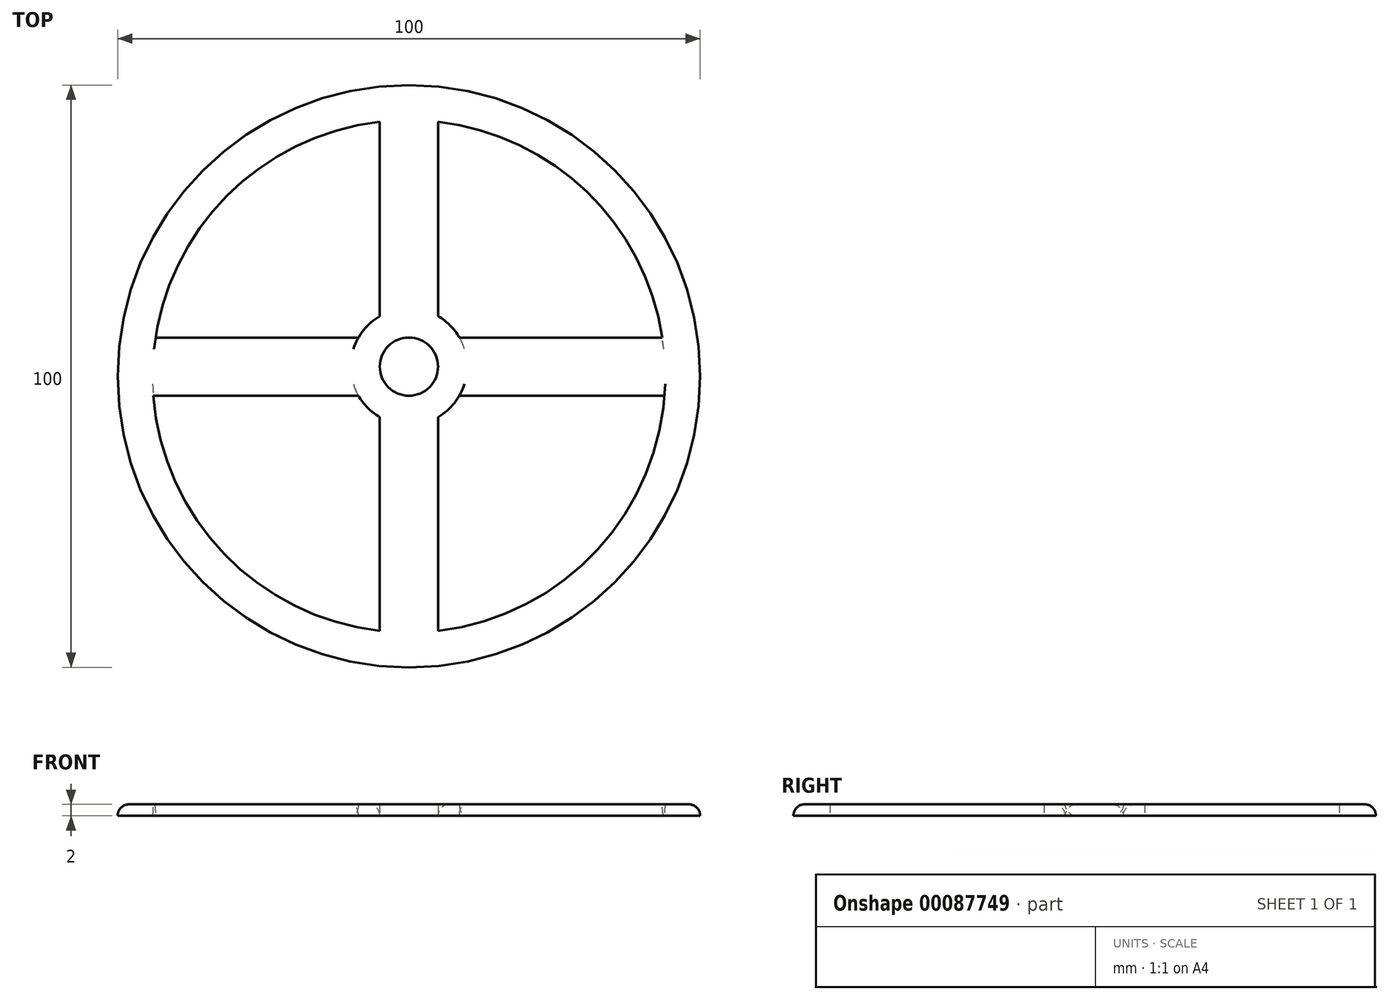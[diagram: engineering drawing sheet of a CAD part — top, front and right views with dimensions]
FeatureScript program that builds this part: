
annotation { "Feature Type Name" : "Feature", "Feature Type Description" : "" }
export const myFeature = defineFeature(function(context is Context, id is Id, definition is map)
    precondition{}
    {
        {
            var Q0;
            Q0=qCreatedBy(makeId("Top.planeOp"),FACE);
            var sketch = newSketch(context, id + "F0", { "sketchPlane" : qUnion([Q0])});
            skCircle(sketch, "E0", {"center": v(0, -1.66) * mm, "radius": 50 * mm});
            skArc(sketch, "E1.0", {"start": v(-43.87, -5) * mm, "mid": v(-31.7, -32.18) * mm, "end": v(-5, -45.38) * mm});
            skCircle(sketch, "E2", {"center": v(0, 0) * mm, "radius": 5 * mm});
            skLineSegment(sketch, "E3", {"start": v(8.66, -5) * mm, "end": v(43.87, -5) * mm});
            skLineSegment(sketch, "E4", {"start": v(5, -8.66) * mm, "end": v(5, -45.38) * mm});
            skArc(sketch, "E5.0", {"start": v(8.66, 5) * mm, "mid": v(7.07, 7.07) * mm, "end": v(5, 8.66) * mm});
            skArc(sketch, "E6.trimOffspring", {"start": v(-5, 42.05) * mm, "mid": v(-30.51, 30.04) * mm, "end": v(-43.5, 5) * mm});
            skArc(sketch, "E7.trimOffspring", {"start": v(43.5, 5) * mm, "mid": v(30.51, 30.04) * mm, "end": v(5, 42.05) * mm});
            skArc(sketch, "E8.trimOffspring", {"start": v(5, -45.38) * mm, "mid": v(31.7, -32.18) * mm, "end": v(43.87, -5) * mm});
            skLineSegment(sketch, "E9.trimOffspring", {"start": v(-8.66, -5) * mm, "end": v(-43.87, -5) * mm});
            skLineSegment(sketch, "E10.trimOffspring", {"start": v(-5, -8.66) * mm, "end": v(-5, -45.38) * mm});
            skPoint(sketch, "E11.orphan", {"position": v(0, -5) * mm});
            skArc(sketch, "E12.trimOffspring", {"start": v(5, -8.66) * mm, "mid": v(7.07, -7.07) * mm, "end": v(8.66, -5) * mm});
            skArc(sketch, "E13.trimOffspring", {"start": v(-8.66, -5) * mm, "mid": v(-7.07, -7.07) * mm, "end": v(-5, -8.66) * mm});
            skLineSegment(sketch, "E14.trimOffspring", {"start": v(-5, 8.66) * mm, "end": v(-5, 42.05) * mm});
            skLineSegment(sketch, "E15.trimOffspring", {"start": v(-8.66, 5) * mm, "end": v(-43.5, 5) * mm});
            skPoint(sketch, "E16.start.orphan", {"position": v(-5, 0) * mm});
            skLineSegment(sketch, "E17.trimOffspring", {"start": v(8.66, 5) * mm, "end": v(43.5, 5) * mm});
            skLineSegment(sketch, "E18.trimOffspring", {"start": v(5, 8.66) * mm, "end": v(5, 42.05) * mm});
            skArc(sketch, "E19.trimOffspring", {"start": v(-5, 8.66) * mm, "mid": v(-7.07, 7.07) * mm, "end": v(-8.66, 5) * mm});
            skPoint(sketch, "E20.start.orphan", {"position": v(5, 0) * mm});
            skPoint(sketch, "E21.start.orphan", {"position": v(0, 5) * mm});
            skSolve(sketch);
        }
        {
            var Q0;
            Q0=makeQuery(id+"F0.imprint","IMPRINT",FACE,{"disambiguationData":[TD([[makeQuery(id+"F0.imprint","IMPRINT",EDGE,{"derivedFrom":sQuery(id+"F0.wireOp",EDGE,"E0")}),1.0]])]});
            extrude(context, id + "F1", {"entities" : qUnion([Q0]), "depth" : 2 * mm});
        }
        {
            var Q0;
            Q0=makeQuery(id+"F1.opExtrude","CAP_EDGE",EDGE,{"disambiguationData":[OSD([sQuery(id+"F0.wireOp",EDGE,"E0")])],"isStart":false});
            var Q1;
            Q1=makeQuery(id+"F1.opExtrude","CAP_EDGE",EDGE,{"disambiguationData":[OSD([sQuery(id+"F0.wireOp",EDGE,"E17.trimOffspring")])],"isStart":true});
            var Q2;
            Q2=makeQuery(id+"F1.opExtrude","CAP_EDGE",EDGE,{"disambiguationData":[OSD([sQuery(id+"F0.wireOp",EDGE,"E9.trimOffspring")])],"isStart":true});
            var Q3;
            Q3=makeQuery(id+"F1.opExtrude","CAP_EDGE",EDGE,{"disambiguationData":[OSD([sQuery(id+"F0.wireOp",EDGE,"E15.trimOffspring")])],"isStart":false});
            var Q4;
            Q4=makeQuery(id+"F1.opExtrude","CAP_EDGE",EDGE,{"disambiguationData":[OSD([sQuery(id+"F0.wireOp",EDGE,"E3")])],"isStart":false});
            var Q5;
            Q5=makeQuery(id+"F1.opExtrude","CAP_EDGE",EDGE,{"disambiguationData":[OSD([sQuery(id+"F0.wireOp",EDGE,"E2")])],"isStart":false});
            fillet(context, id + "F2", {"entities" : qUnion([Q0, Q1, Q2, Q3, Q4, Q5]), "radius" : 2 * mm, "tangentPropagation" : true, "allowEdgeOverflow" : false});
        }
    });
